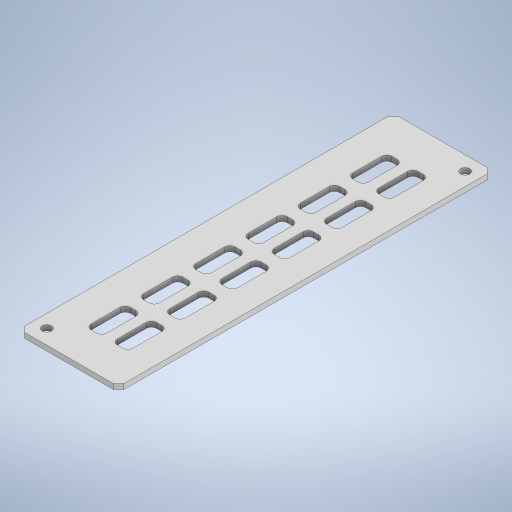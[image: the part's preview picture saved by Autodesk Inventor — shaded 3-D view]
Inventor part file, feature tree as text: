
AUTODESK INVENTOR PART (.ipt)
format: ipt  version: 2024 (Build 280153020, 153B)  size: 379,904 bytes
history: native  units: mm
features: extrude x4, sketch x4, pattern_linear x2, chamfer x1
ambient origin geometry x8: Origin, YZ Plane, XZ Plane, XY Plane, X Axis, Y Axis, Z Axis, Center Point
bodies: Solid1 (feature_tree)
feature tree (11):
  extrude  "Extrusion1"  Depth=143.0mm
  extrude  "Extrusion2"  Depth=2.0mm
  extrude  "Extrusion3"  TaperAngle=0.0deg  [1 undecoded]
  extrude  "Extrusion4"  TaperAngle=180.0deg  [1 undecoded]
  pattern_linear  "Rectangular Pattern1"  Spacing1=3.5mm  [1 undecoded]
  pattern_linear  "Rectangular Pattern2"  Spacing1=3.5mm  [1 undecoded]
  chamfer  "Chamfer1"  Distance=14.75mm
  sketch  "Sketch1"  dims[d0=38.0mm d1=143.0mm]
  sketch  "Sketch2"  dims[d2=2.0mm d3=0.0mm d4=5.5mm]
  sketch  "Sketch3"  dims[d7=5.0mm d8=0.0mm]
  sketch  "Sketch4"  dims[d9=5.5mm d12=180.0deg d13=3.5mm d14=3.5mm d15=14.75mm d16=0.0mm d17=29.5mm d18=2.0mm d19=25.0mm d20=25.0mm d21=2.0mm d22=0.0mm d23=3.0mm d24=3.0mm d25=6.0mm d26=6.0mm d27=3.0mm d28=15.0mm d29=2.0mm d30=2.0mm d31=0.0mm d32=40.0mm d34=20.0mm d35=20.0mm d37=10.0mm d38=30.0mm d40=20.0mm d41=20.0mm d43=10.0mm d44=2.0mm d45=2.0mm d46=45.0deg]
note: 4 required parameter values undecoded (feature->parameter linkage not recoverable at this tier; creation-order binding heuristic only, values carry confidence <= 0.55)
